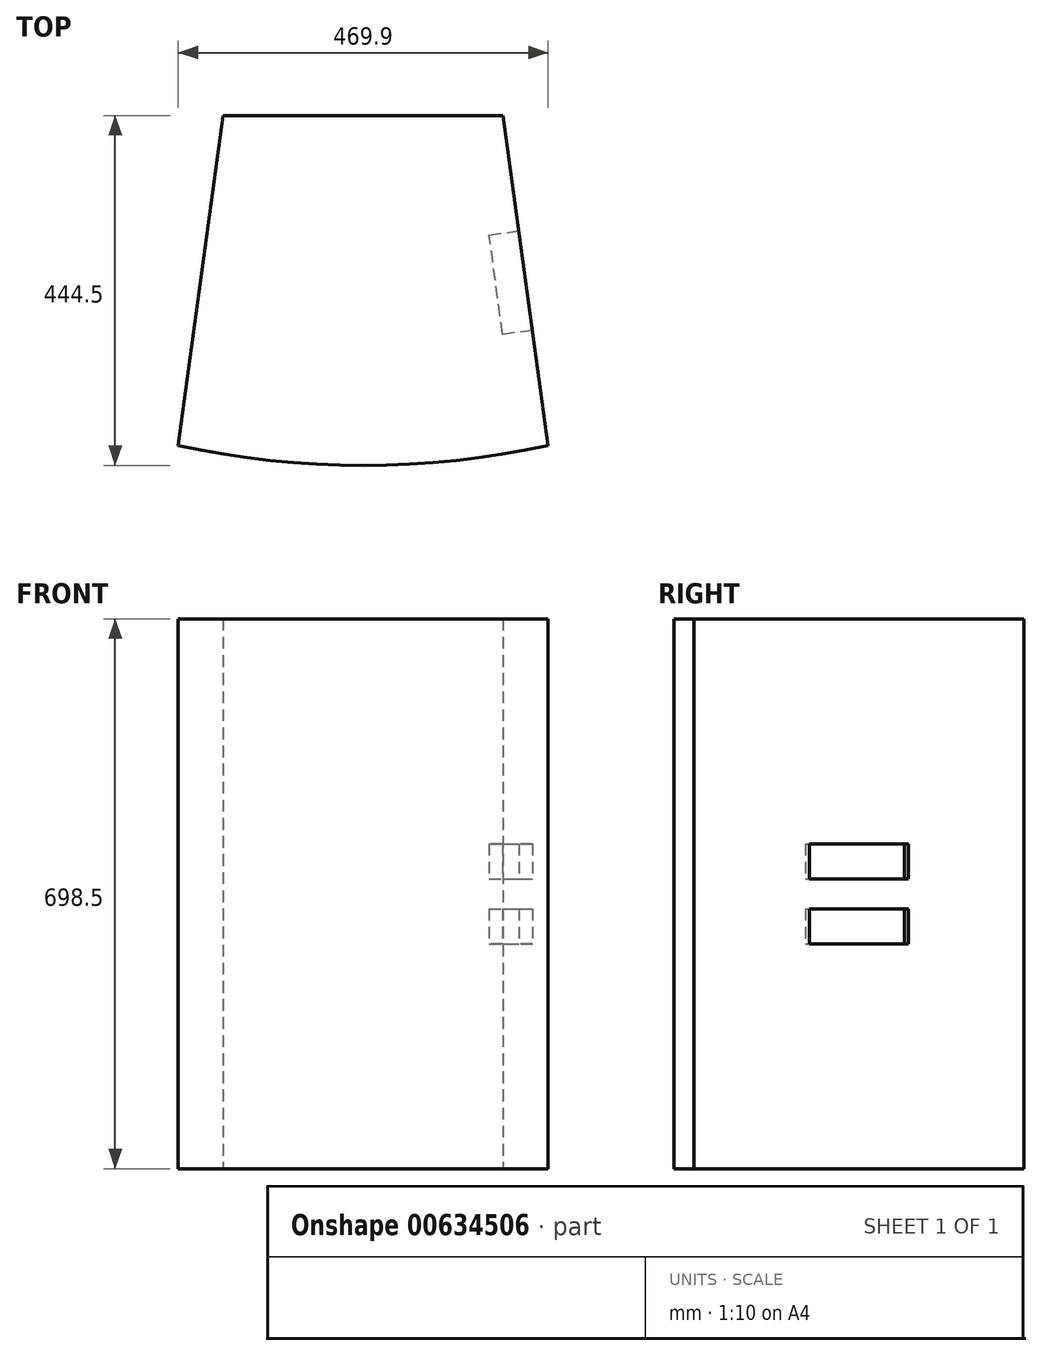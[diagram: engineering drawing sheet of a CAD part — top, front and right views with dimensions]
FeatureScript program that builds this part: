
annotation { "Feature Type Name" : "Feature", "Feature Type Description" : "" }
export const myFeature = defineFeature(function(context is Context, id is Id, definition is map)
    precondition{}
    {
        {
            var Q0;
            Q0=qCreatedBy(makeId("Top.planeOp"),FACE);
            var sketch = newSketch(context, id + "F0", { "sketchPlane" : qUnion([Q0])});
            skLineSegment(sketch, "E0", {"start": v(-177.8, 0) * mm, "end": v(177.8, 0) * mm});
            skLineSegment(sketch, "E1", {"start": v(-177.8, 0) * mm, "end": v(-234.95, -419.1) * mm});
            skLineSegment(sketch, "E2", {"start": v(0, 0) * mm, "end": v(0, -444.5) * mm, "construction": true});
            skLineSegment(sketch, "E3", {"start": v(234.95, -419.1) * mm, "end": v(177.8, 0) * mm});
            skArc(sketch, "E4", {"start": v(-234.95, -419.1) * mm, "mid": v(0, -444.5) * mm, "end": v(234.95, -419.1) * mm});
            skLineSegment(sketch, "E5", {"start": v(-234.95, -419.1) * mm, "end": v(234.95, -419.1) * mm, "construction": true});
            skSolve(sketch);
        }
        {
            var Q0;
            Q0=makeQuery(id+"F0.imprint","IMPRINT",FACE,{"disambiguationData":[TD([[makeQuery(id+"F0.imprint","IMPRINT",EDGE,{"derivedFrom":sQuery(id+"F0.wireOp",EDGE,"E0")}),-1.0]])]});
            extrude(context, id + "F1", {"entities" : qUnion([Q0]), "offsetDistance" : 25.4 * mm, "depth" : 698.5 * mm});
        }
        {
            var Q0;
            Q0=makeQuery(id+"F1.opExtrude","SWEPT_FACE",FACE,{"disambiguationData":[OSD([sQuery(id+"F0.wireOp",EDGE,"E3")])]});
            var sketch = newSketch(context, id + "F2", { "sketchPlane" : qUnion([Q0])});
            skLineSegment(sketch, "E6.bottom", {"start": v(-299.01, 412.75) * mm, "end": v(-172.01, 412.75) * mm});
            skLineSegment(sketch, "E6.top", {"start": v(-299.01, 285.75) * mm, "end": v(-172.01, 285.75) * mm});
            skLineSegment(sketch, "E6.left", {"start": v(-299.01, 412.75) * mm, "end": v(-299.01, 285.75) * mm});
            skLineSegment(sketch, "E6.right", {"start": v(-172.01, 412.75) * mm, "end": v(-172.01, 285.75) * mm});
            skPoint(sketch, "E6.middle", {"position": v(-235.51, 349.25) * mm});
            skLineSegment(sketch, "E7.bottom", {"start": v(-172.01, 368.3) * mm, "end": v(-299.01, 368.3) * mm});
            skLineSegment(sketch, "E7.top", {"start": v(-172.01, 330.2) * mm, "end": v(-299.01, 330.2) * mm});
            skLineSegment(sketch, "E7.left", {"start": v(-172.01, 368.3) * mm, "end": v(-172.01, 330.2) * mm});
            skLineSegment(sketch, "E7.right", {"start": v(-299.01, 368.3) * mm, "end": v(-299.01, 330.2) * mm});
            skSolve(sketch);
        }
        {
            var Q0;
            {var subQ0=sQuery(id+"F2.wireOp",EDGE,"E6.top");Q0=makeQuery(id+"F2.imprint","IMPRINT",FACE,{"disambiguationData":[TD([[makeQuery(id+"F2.imprint","IMPRINT",EDGE,{"derivedFrom":subQ0}),1.0]])]});}
            var Q1;
            {var subQ0=sQuery(id+"F2.wireOp",EDGE,"E6.bottom");Q1=makeQuery(id+"F2.imprint","IMPRINT",FACE,{"disambiguationData":[TD([[makeQuery(id+"F2.imprint","IMPRINT",EDGE,{"derivedFrom":subQ0}),-1.0]])]});}
            extrude(context, id + "F3", {"entities" : qUnion([Q0, Q1]), "operationType" : NewBodyOperationType.REMOVE, "oppositeDirection" : true, "depth" : 38.1 * mm, "offsetDistance" : 25.4 * mm});
        }
    });
